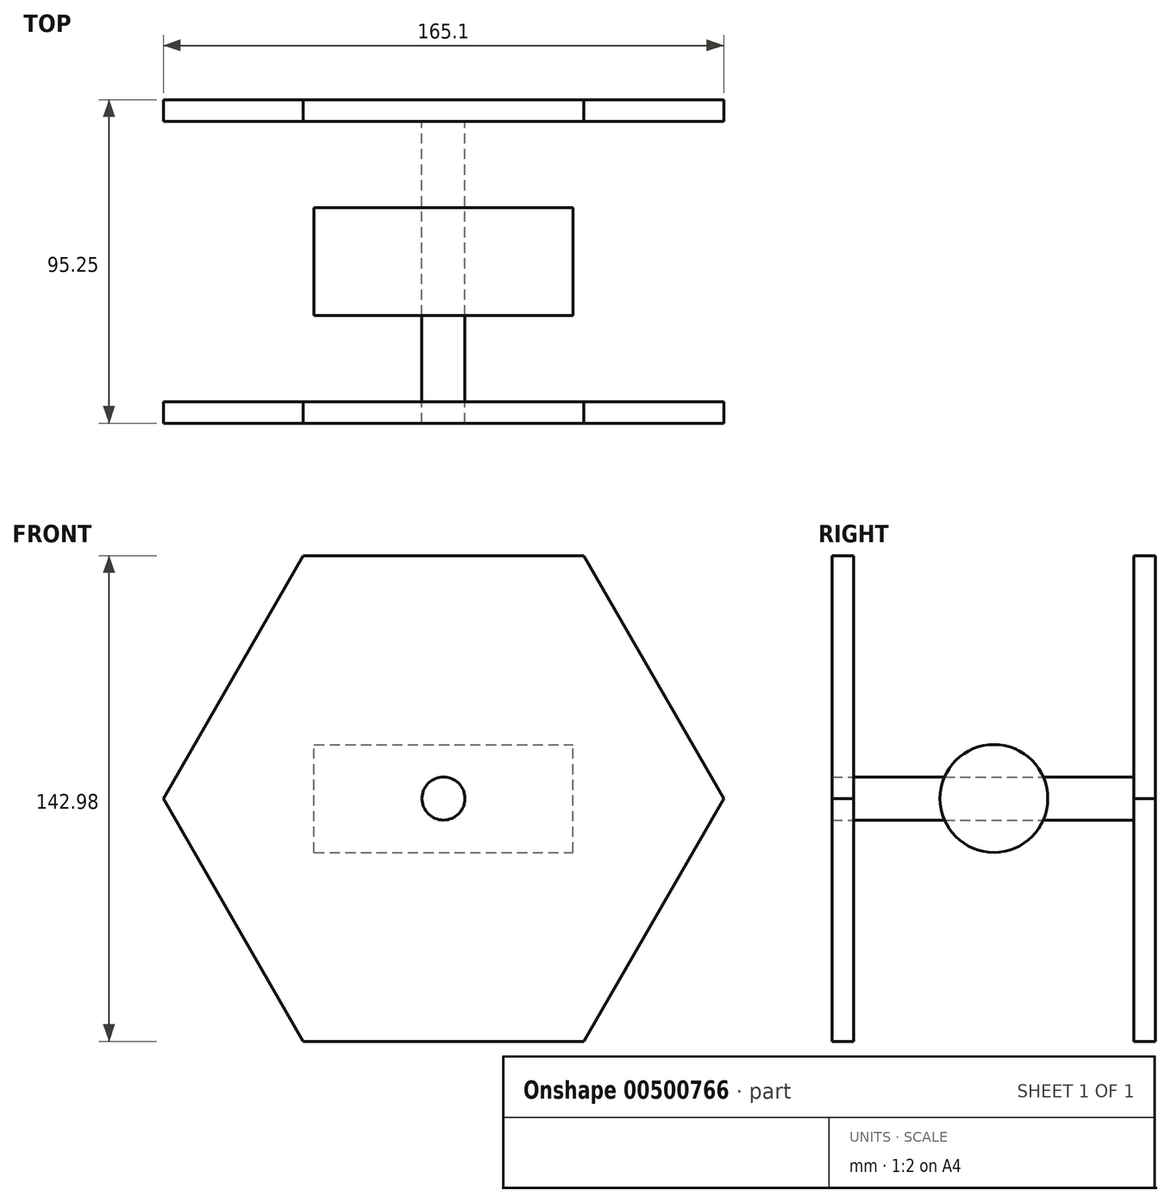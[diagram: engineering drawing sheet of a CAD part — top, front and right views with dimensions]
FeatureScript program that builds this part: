
annotation { "Feature Type Name" : "Feature", "Feature Type Description" : "" }
export const myFeature = defineFeature(function(context is Context, id is Id, definition is map)
    precondition{}
    {
        {
            var Q0;
            Q0=qCreatedBy(makeId("Front.planeOp"),FACE);
            var sketch = newSketch(context, id + "F0", { "sketchPlane" : qUnion([Q0])});
            skCircle(sketch, "E0", {"center": v(0, 0) * mm, "radius": 6.35 * mm});
            skSolve(sketch);
        }
        {
            var Q0;
            Q0 = qSketchRegion(id + "F0", true);
            extrude(context, id + "F1", {"entities" : qUnion([Q0]), "depth" : 82.55 * mm, "offsetDistance" : 25.4 * mm});
        }
        {
            var Q0;
            Q0=makeQuery(id+"F1.opExtrude","CAP_FACE",FACE,{"disambiguationData":[OSD([sQuery(id+"F0.wireOp",EDGE,"E0")])],"isStart":false});
            var sketch = newSketch(context, id + "F2", { "sketchPlane" : qUnion([Q0])});
            skLineSegment(sketch, "E1", {"start": v(-41.28, 71.5) * mm, "end": v(41.27, 71.5) * mm});
            skLineSegment(sketch, "E2", {"start": v(41.28, 71.5) * mm, "end": v(82.55, 0) * mm});
            skLineSegment(sketch, "E3", {"start": v(82.55, 0) * mm, "end": v(41.27, -71.5) * mm});
            skLineSegment(sketch, "E4", {"start": v(41.27, -71.5) * mm, "end": v(-41.28, -71.5) * mm});
            skLineSegment(sketch, "E5", {"start": v(-41.28, -71.5) * mm, "end": v(-82.55, 0) * mm});
            skLineSegment(sketch, "E6", {"start": v(-82.55, 0) * mm, "end": v(-41.27, 71.5) * mm});
            skCircle(sketch, "E7.0", {"center": v(0, 0) * mm, "radius": 6.35 * mm});
            skSolve(sketch);
        }
        {
            var Q0;
            Q0 = qSketchRegion(id + "F2", true);
            extrude(context, id + "F3", {"entities" : qUnion([Q0]), "depth" : 6.35 * mm, "offsetDistance" : 25.4 * mm});
        }
        {
            var Q0;
            Q0=makeQuery(id+"F1.opExtrude","CAP_FACE",FACE,{"disambiguationData":[OSD([sQuery(id+"F0.wireOp",EDGE,"E0")])],"isStart":true});
            var sketch = newSketch(context, id + "F4", { "sketchPlane" : qUnion([Q0])});
            skLineSegment(sketch, "E8.0", {"start": v(41.28, 71.5) * mm, "end": v(-41.27, 71.5) * mm});
            skLineSegment(sketch, "E9.0", {"start": v(-41.28, 71.5) * mm, "end": v(-82.55, 0) * mm});
            skLineSegment(sketch, "E10.0", {"start": v(-82.55, 0) * mm, "end": v(-41.27, -71.5) * mm});
            skLineSegment(sketch, "E11.0", {"start": v(-41.27, -71.5) * mm, "end": v(41.28, -71.5) * mm});
            skLineSegment(sketch, "E12.0", {"start": v(41.28, -71.5) * mm, "end": v(82.55, 0) * mm});
            skLineSegment(sketch, "E13.0", {"start": v(82.55, 0) * mm, "end": v(41.27, 71.5) * mm});
            skSolve(sketch);
        }
        {
            var Q0;
            Q0 = qSketchRegion(id + "F4", true);
            extrude(context, id + "F5", {"entities" : qUnion([Q0]), "depth" : 6.35 * mm, "offsetDistance" : 25.4 * mm});
        }
        {
            var Q0;
            Q0=qCreatedBy(makeId("Right.planeOp"),FACE);
            var sketch = newSketch(context, id + "F6", { "sketchPlane" : qUnion([Q0])});
            skCircle(sketch, "E14", {"center": v(-41.28, 0) * mm, "radius": 15.88 * mm});
            skSolve(sketch);
        }
        {
            var Q0;
            Q0 = qSketchRegion(id + "F6", true);
            extrude(context, id + "F7", {"entities" : qUnion([Q0]), "endBound" : BoundingType.SYMMETRIC, "oppositeDirection" : true, "depth" : 76.2 * mm, "offsetDistance" : 25.4 * mm});
        }
    });
